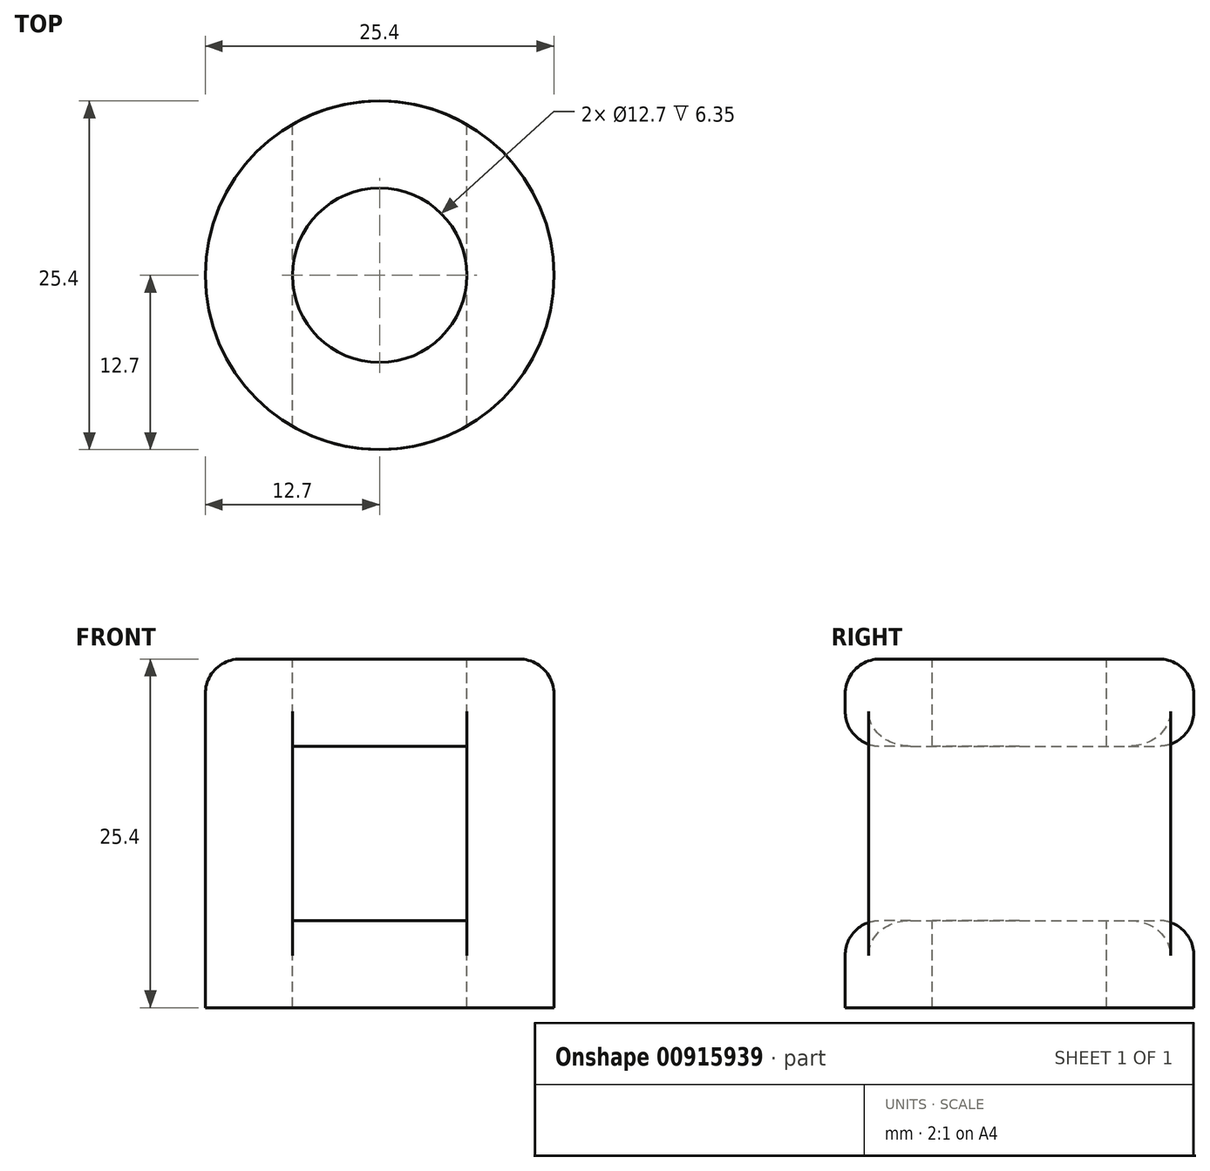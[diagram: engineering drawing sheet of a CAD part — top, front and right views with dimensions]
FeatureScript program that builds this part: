
annotation { "Feature Type Name" : "Feature", "Feature Type Description" : "" }
export const myFeature = defineFeature(function(context is Context, id is Id, definition is map)
    precondition{}
    {
        {
            var Q0;
            Q0=qCreatedBy(makeId("Top.planeOp"),FACE);
            var sketch = newSketch(context, id + "F0", { "sketchPlane" : qUnion([Q0])});
            skLineSegment(sketch, "E0.bottom", {"start": v(-12.7, -12.7) * mm, "end": v(12.7, -12.7) * mm});
            skLineSegment(sketch, "E0.top", {"start": v(-12.7, 12.7) * mm, "end": v(12.7, 12.7) * mm});
            skLineSegment(sketch, "E0.left", {"start": v(-12.7, -12.7) * mm, "end": v(-12.7, 12.7) * mm});
            skLineSegment(sketch, "E0.right", {"start": v(12.7, -12.7) * mm, "end": v(12.7, 12.7) * mm});
            skLineSegment(sketch, "E1", {"start": v(-12.7, 12.7) * mm, "end": v(12.7, -12.7) * mm});
            skLineSegment(sketch, "E2", {"start": v(-12.7, -12.7) * mm, "end": v(12.7, 12.7) * mm});
            skPoint(sketch, "E3", {"position": v(0, 0) * mm});
            skCircle(sketch, "E4", {"center": v(0, 0) * mm, "radius": 12.7 * mm});
            skSolve(sketch);
        }
        {
            var Q0;
            {var subQ0=sQuery(id+"F0.wireOp",EDGE,"E2");var subQ1=sQuery(id+"F0.wireOp",EDGE,"E1");var subQ2=makeQuery(id+"F0.imprint","INTERSECT",VERTEX,{"derivedFrom":[subQ1,subQ0]});Q0=makeQuery(id+"F0.imprint","IMPRINT",FACE,{"disambiguationData":[TD([[makeQuery(id+"F0.imprint","IMPRINT",EDGE,{"disambiguationData":[TD([[subQ2,-1.0]])],"derivedFrom":subQ1}),-1.0]])]});}
            var Q1;
            {var subQ0=sQuery(id+"F0.wireOp",EDGE,"E2");var subQ1=sQuery(id+"F0.wireOp",EDGE,"E1");var subQ2=makeQuery(id+"F0.imprint","INTERSECT",VERTEX,{"derivedFrom":[subQ1,subQ0]});Q1=makeQuery(id+"F0.imprint","IMPRINT",FACE,{"disambiguationData":[TD([[makeQuery(id+"F0.imprint","IMPRINT",EDGE,{"disambiguationData":[TD([[subQ2,-1.0]])],"derivedFrom":subQ1}),1.0]])]});}
            var Q2;
            {var subQ0=sQuery(id+"F0.wireOp",EDGE,"E4");var subQ1=sQuery(id+"F0.wireOp",EDGE,"E1");var subQ2=makeQuery(id+"F0.imprint","INTERSECT",VERTEX,{"disambiguationData":[OD(0.0)],"derivedFrom":[subQ1,subQ0]});Q2=makeQuery(id+"F0.imprint","IMPRINT",FACE,{"disambiguationData":[TD([[makeQuery(id+"F0.imprint","IMPRINT",EDGE,{"disambiguationData":[TD([[subQ2,-1.0]])],"derivedFrom":subQ1}),1.0]])]});}
            var Q3;
            {var subQ0=sQuery(id+"F0.wireOp",EDGE,"E4");var subQ1=sQuery(id+"F0.wireOp",EDGE,"E1");var subQ2=makeQuery(id+"F0.imprint","INTERSECT",VERTEX,{"disambiguationData":[OD(0.0)],"derivedFrom":[subQ1,subQ0]});Q3=makeQuery(id+"F0.imprint","IMPRINT",FACE,{"disambiguationData":[TD([[makeQuery(id+"F0.imprint","IMPRINT",EDGE,{"disambiguationData":[TD([[subQ2,-1.0]])],"derivedFrom":subQ1}),-1.0]])]});}
            extrude(context, id + "F1", {"entities" : qUnion([Q0, Q1, Q2, Q3]), "depth" : 25.4 * mm, "offsetDistance" : 25.4 * mm});
        }
        {
            var Q0;
            Q0=makeQuery(id+"F1.opExtrude","CAP_FACE",FACE,{"disambiguationData":[OSD([sQuery(id+"F0.wireOp",EDGE,"E4")])],"isStart":false});
            var sketch = newSketch(context, id + "F2", { "sketchPlane" : qUnion([Q0])});
            skCircle(sketch, "E5.0.0", {"center": v(0, 0) * mm, "radius": 12.7 * mm});
            skCircle(sketch, "E6", {"center": v(0, 0) * mm, "radius": 6.35 * mm});
            skSolve(sketch);
        }
        {
            var Q0;
            Q0=makeQuery(id+"F2.imprint","IMPRINT",FACE,{"disambiguationData":[TD([[makeQuery(id+"F2.imprint","IMPRINT",EDGE,{"derivedFrom":sQuery(id+"F2.wireOp",EDGE,"E6")}),1.0]])]});
            extrude(context, id + "F3", {"entities" : qUnion([Q0]), "operationType" : NewBodyOperationType.REMOVE, "endBound" : BoundingType.THROUGH_ALL, "oppositeDirection" : true, "depth" : 25.4 * mm, "offsetDistance" : 25.4 * mm});
        }
        {
            var Q0;
            Q0=qCreatedBy(makeId("Front.planeOp"),FACE);
            var sketch = newSketch(context, id + "F4", { "sketchPlane" : qUnion([Q0])});
            skLineSegment(sketch, "E7.bottom", {"start": v(-6.35, 19.05) * mm, "end": v(6.35, 19.05) * mm});
            skLineSegment(sketch, "E7.top", {"start": v(-6.35, 6.35) * mm, "end": v(6.35, 6.35) * mm});
            skLineSegment(sketch, "E7.left", {"start": v(-6.35, 19.05) * mm, "end": v(-6.35, 6.35) * mm});
            skLineSegment(sketch, "E7.right", {"start": v(6.35, 19.05) * mm, "end": v(6.35, 6.35) * mm});
            skLineSegment(sketch, "E8", {"start": v(-6.35, 0) * mm, "end": v(-6.35, 25.4) * mm});
            skLineSegment(sketch, "E9", {"start": v(6.35, 25.4) * mm, "end": v(6.35, 0) * mm});
            skLineSegment(sketch, "E10.0.0", {"start": v(-12.7, 25.4) * mm, "end": v(12.7, 25.4) * mm});
            skSolve(sketch);
        }
        {
            var Q0;
            {var subQ0=sQuery(id+"F4.wireOp",EDGE,"E7.bottom");Q0=makeQuery(id+"F4.imprint","IMPRINT",FACE,{"disambiguationData":[TD([[makeQuery(id+"F4.imprint","IMPRINT",EDGE,{"derivedFrom":subQ0}),-1.0]])]});}
            extrude(context, id + "F5", {"entities" : qUnion([Q0]), "operationType" : NewBodyOperationType.REMOVE, "endBound" : BoundingType.SYMMETRIC, "depth" : 61.72 * mm, "offsetDistance" : 25.4 * mm});
        }
        {
            var Q0;
            Q0=makeQuery(id+"F5.boolean.opBoolean","INTERSECT",EDGE,{"disambiguationData":[OD(1.0)],"derivedFrom":[makeQuery(id+"F1.opExtrude","SWEPT_FACE",FACE,{"disambiguationData":[OSD([sQuery(id+"F0.wireOp",EDGE,"E4")])]}),makeQuery(id+"F5.opExtrude","SWEPT_FACE",FACE,{"disambiguationData":[OSD([sQuery(id+"F4.wireOp",EDGE,"E7.bottom")])]})]});
            var Q1;
            Q1=makeQuery(id+"F5.boolean.opBoolean","INTERSECT",EDGE,{"disambiguationData":[OD(1.0)],"derivedFrom":[makeQuery(id+"F1.opExtrude","SWEPT_FACE",FACE,{"disambiguationData":[OSD([sQuery(id+"F0.wireOp",EDGE,"E4")])]}),makeQuery(id+"F5.opExtrude","SWEPT_FACE",FACE,{"disambiguationData":[OSD([sQuery(id+"F4.wireOp",EDGE,"E7.top")])]})]});
            var Q2;
            Q2=makeQuery(id+"F5.boolean.opBoolean","INTERSECT",EDGE,{"disambiguationData":[OD(1.0)],"derivedFrom":[makeQuery(id+"F1.opExtrude","SWEPT_FACE",FACE,{"disambiguationData":[OSD([sQuery(id+"F0.wireOp",EDGE,"E4")])]}),makeQuery(id+"F5.opExtrude","SWEPT_FACE",FACE,{"disambiguationData":[OSD([sQuery(id+"F4.wireOp",EDGE,"E8")])]})]});
            var Q3;
            Q3=makeQuery(id+"F5.boolean.opBoolean","INTERSECT",EDGE,{"disambiguationData":[OD(1.0)],"derivedFrom":[makeQuery(id+"F1.opExtrude","SWEPT_FACE",FACE,{"disambiguationData":[OSD([sQuery(id+"F0.wireOp",EDGE,"E4")])]}),makeQuery(id+"F5.opExtrude","SWEPT_FACE",FACE,{"disambiguationData":[OSD([sQuery(id+"F4.wireOp",EDGE,"E9")])]})]});
            var Q4;
            Q4=makeQuery(id+"F1.opExtrude","CAP_EDGE",EDGE,{"disambiguationData":[OSD([sQuery(id+"F0.wireOp",EDGE,"E4")])],"isStart":false});
            var Q5;
            Q5=makeQuery(id+"F5.boolean.opBoolean","INTERSECT",EDGE,{"disambiguationData":[OD(0.0)],"derivedFrom":[makeQuery(id+"F1.opExtrude","SWEPT_FACE",FACE,{"disambiguationData":[OSD([sQuery(id+"F0.wireOp",EDGE,"E4")])]}),makeQuery(id+"F5.opExtrude","SWEPT_FACE",FACE,{"disambiguationData":[OSD([sQuery(id+"F4.wireOp",EDGE,"E7.bottom")])]})]});
            var Q6;
            Q6=makeQuery(id+"F5.boolean.opBoolean","INTERSECT",EDGE,{"disambiguationData":[OD(0.0)],"derivedFrom":[makeQuery(id+"F1.opExtrude","SWEPT_FACE",FACE,{"disambiguationData":[OSD([sQuery(id+"F0.wireOp",EDGE,"E4")])]}),makeQuery(id+"F5.opExtrude","SWEPT_FACE",FACE,{"disambiguationData":[OSD([sQuery(id+"F4.wireOp",EDGE,"E8")])]})]});
            var Q7;
            Q7=makeQuery(id+"F5.boolean.opBoolean","INTERSECT",EDGE,{"disambiguationData":[OD(0.0)],"derivedFrom":[makeQuery(id+"F1.opExtrude","SWEPT_FACE",FACE,{"disambiguationData":[OSD([sQuery(id+"F0.wireOp",EDGE,"E4")])]}),makeQuery(id+"F5.opExtrude","SWEPT_FACE",FACE,{"disambiguationData":[OSD([sQuery(id+"F4.wireOp",EDGE,"E7.top")])]})]});
            var Q8;
            Q8=makeQuery(id+"F5.boolean.opBoolean","INTERSECT",EDGE,{"disambiguationData":[OD(0.0)],"derivedFrom":[makeQuery(id+"F1.opExtrude","SWEPT_FACE",FACE,{"disambiguationData":[OSD([sQuery(id+"F0.wireOp",EDGE,"E4")])]}),makeQuery(id+"F5.opExtrude","SWEPT_FACE",FACE,{"disambiguationData":[OSD([sQuery(id+"F4.wireOp",EDGE,"E9")])]})]});
            var Q9;
            Q9=makeQuery(id+"F3.boolean.opBoolean","COPY",EDGE,{"derivedFrom":makeQuery(id+"F3.opExtrude","CAP_EDGE",EDGE,{"disambiguationData":[OSD([sQuery(id+"F2.wireOp",EDGE,"E6")])],"isStart":true})});
            fillet(context, id + "F6", {"entities" : qUnion([Q0, Q1, Q2, Q3, Q4, Q5, Q6, Q7, Q8, Q9]), "radius" : 2.54 * mm, "tangentPropagation" : true, "allowEdgeOverflow" : false});
        }
    });
